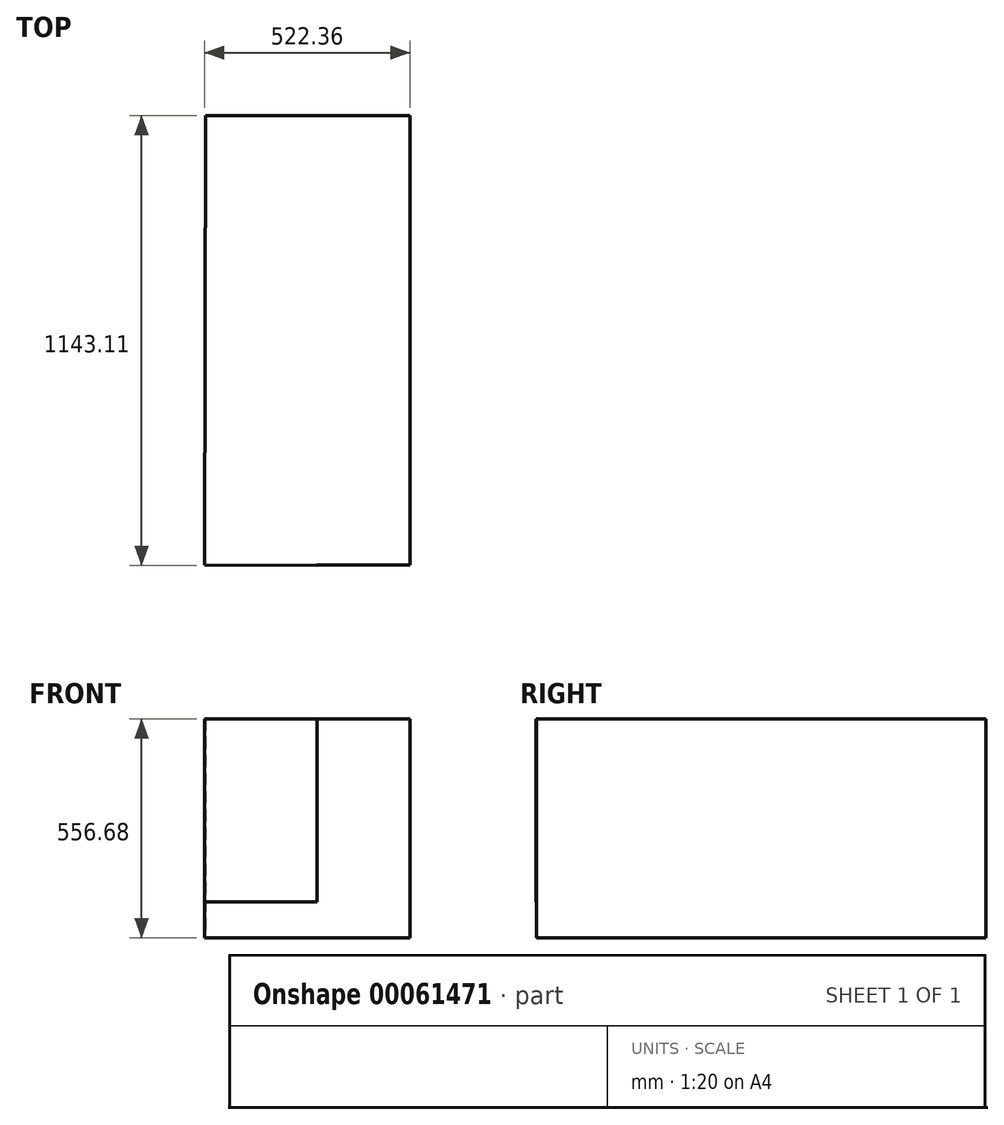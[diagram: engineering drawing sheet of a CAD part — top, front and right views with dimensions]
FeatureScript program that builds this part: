
annotation { "Feature Type Name" : "Feature", "Feature Type Description" : "" }
export const myFeature = defineFeature(function(context is Context, id is Id, definition is map)
    precondition{}
    {
        {
            var Q0;
            Q0=qCreatedBy(makeId("Top.planeOp"),FACE);
            var sketch = newSketch(context, id + "F0", { "sketchPlane" : qUnion([Q0])});
            skLineSegment(sketch, "E0.MirrorCS", {"start": v(260.35, 590.45) * mm, "end": v(260.35, -552.55) * mm});
            skLineSegment(sketch, "E1.MirrorCS", {"start": v(152.4, 742.85) * mm, "end": v(368.3, 666.65) * mm});
            skLineSegment(sketch, "E2", {"start": v(-484.24, -552.55) * mm, "end": v(-484.24, -1085.95) * mm});
            skLineSegment(sketch, "E3.MirrorCS", {"start": v(260.35, -552.55) * mm, "end": v(0, -552.55) * mm});
            skLineSegment(sketch, "E4.MirrorCS", {"start": v(484.24, -552.55) * mm, "end": v(484.24, -1085.95) * mm});
            skLineSegment(sketch, "E5", {"start": v(0, 590.45) * mm, "end": v(-260.35, 590.45) * mm});
            skLineSegment(sketch, "E6", {"start": v(-260.35, -552.55) * mm, "end": v(0, -552.55) * mm});
            skLineSegment(sketch, "E7.MirrorCS", {"start": v(484.24, -1085.95) * mm, "end": v(0, -1085.95) * mm});
            skLineSegment(sketch, "E8", {"start": v(-260.35, 590.45) * mm, "end": v(-260.35, -552.55) * mm});
            skLineSegment(sketch, "E9", {"start": v(-444.5, 444.4) * mm, "end": v(-352.42, -63.6) * mm});
            skLineSegment(sketch, "E10", {"start": v(0, 742.85) * mm, "end": v(0, 590.45) * mm});
            skLineSegment(sketch, "E11.MirrorCS", {"start": v(352.42, -63.6) * mm, "end": v(484.24, -552.55) * mm});
            skLineSegment(sketch, "E12", {"start": v(-368.3, 666.65) * mm, "end": v(-444.5, 444.4) * mm});
            skLineSegment(sketch, "E13.MirrorCS", {"start": v(0, 742.85) * mm, "end": v(152.4, 742.85) * mm});
            skLineSegment(sketch, "E14", {"start": v(-152.4, 742.85) * mm, "end": v(-368.3, 666.65) * mm});
            skLineSegment(sketch, "E15", {"start": v(0, -552.55) * mm, "end": v(0, -1085.95) * mm});
            skLineSegment(sketch, "E16", {"start": v(0, 742.85) * mm, "end": v(-152.4, 742.85) * mm});
            skLineSegment(sketch, "E17", {"start": v(-484.24, -1085.95) * mm, "end": v(0, -1085.95) * mm});
            skLineSegment(sketch, "E18.MirrorCS", {"start": v(0, 590.45) * mm, "end": v(260.35, 590.45) * mm});
            skLineSegment(sketch, "E19.MirrorCS", {"start": v(368.3, 666.65) * mm, "end": v(444.5, 444.4) * mm});
            skLineSegment(sketch, "E20", {"start": v(0, 742.85) * mm, "end": v(0, -585.87) * mm, "construction": true});
            skLineSegment(sketch, "E21", {"start": v(-352.42, -63.6) * mm, "end": v(-484.24, -552.55) * mm});
            skLineSegment(sketch, "E22.MirrorCS", {"start": v(444.5, 444.4) * mm, "end": v(352.42, -63.6) * mm});
            skSolve(sketch);
        }
        {
            var Q0;
            Q0=makeQuery(id+"F0.imprint","IMPRINT",FACE,{"disambiguationData":[TD([[makeQuery(id+"F0.imprint","IMPRINT",EDGE,{"derivedFrom":sQuery(id+"F0.wireOp",EDGE,"E0.MirrorCS")}),-1.0]])]});
            var sketch = newSketch(context, id + "F1", { "sketchPlane" : qUnion([Q0])});
            skLineSegment(sketch, "E23", {"start": v(-259.87, 590.71) * mm, "end": v(260.45, 590.71) * mm});
            skLineSegment(sketch, "E24", {"start": v(260.45, 590.71) * mm, "end": v(260.45, -551.89) * mm});
            skLineSegment(sketch, "E25", {"start": v(260.45, -551.89) * mm, "end": v(-261.91, -551.89) * mm});
            skLineSegment(sketch, "E26", {"start": v(-261.91, -551.89) * mm, "end": v(-259.87, 590.71) * mm});
            skSolve(sketch);
        }
        {
            var Q0;
            Q0 = qSketchRegion(id + "F1", true);
            extrude(context, id + "F2", {"entities" : qUnion([Q0]), "depth" : 556.68 * mm});
        }
        {
            var Q0;
            Q0=makeQuery(id+"F2.opExtrude","SWEPT_FACE",FACE,{"disambiguationData":[OSD([sQuery(id+"F1.wireOp",EDGE,"E26")])]});
            var sketch = newSketch(context, id + "F3", { "sketchPlane" : qUnion([Q0])});
            skLineSegment(sketch, "E27", {"start": v(-590.25, 0) * mm, "end": v(-440.18, 145.98) * mm});
            skLineSegment(sketch, "E28", {"start": v(-440.18, 145.98) * mm, "end": v(-280.84, 235.25) * mm});
            skLineSegment(sketch, "E29", {"start": v(-280.84, 235.25) * mm, "end": v(-162.25, 235.25) * mm});
            skLineSegment(sketch, "E30", {"start": v(-162.25, 235.25) * mm, "end": v(0, 361.52) * mm});
            skLineSegment(sketch, "E31", {"start": v(0, 361.52) * mm, "end": v(210.4, 361.52) * mm});
            skLineSegment(sketch, "E32", {"start": v(210.4, 361.52) * mm, "end": v(210.4, 92.23) * mm});
            skLineSegment(sketch, "E33", {"start": v(210.4, 92.23) * mm, "end": v(552.36, 92.23) * mm});
            skLineSegment(sketch, "E34", {"start": v(552.36, 92.23) * mm, "end": v(552.36, 0) * mm});
            skLineSegment(sketch, "E35", {"start": v(552.36, 0) * mm, "end": v(-590.25, 0) * mm});
            skLineSegment(sketch, "E36", {"start": v(-590.25, 0) * mm, "end": v(552.36, 0) * mm});
            skSolve(sketch);
        }
        {
            var Q0;
            Q0=makeQuery(id+"F3.imprint","IMPRINT",FACE,{"disambiguationData":[TD([[makeQuery(id+"F3.imprint","IMPRINT",EDGE,{"derivedFrom":sQuery(id+"F3.wireOp",EDGE,"E27")}),1.0]])]});
            extrude(context, id + "F4", {"entities" : qUnion([Q0]), "operationType" : NewBodyOperationType.ADD, "oppositeDirection" : true, "depth" : 286.25 * mm});
        }
    });
